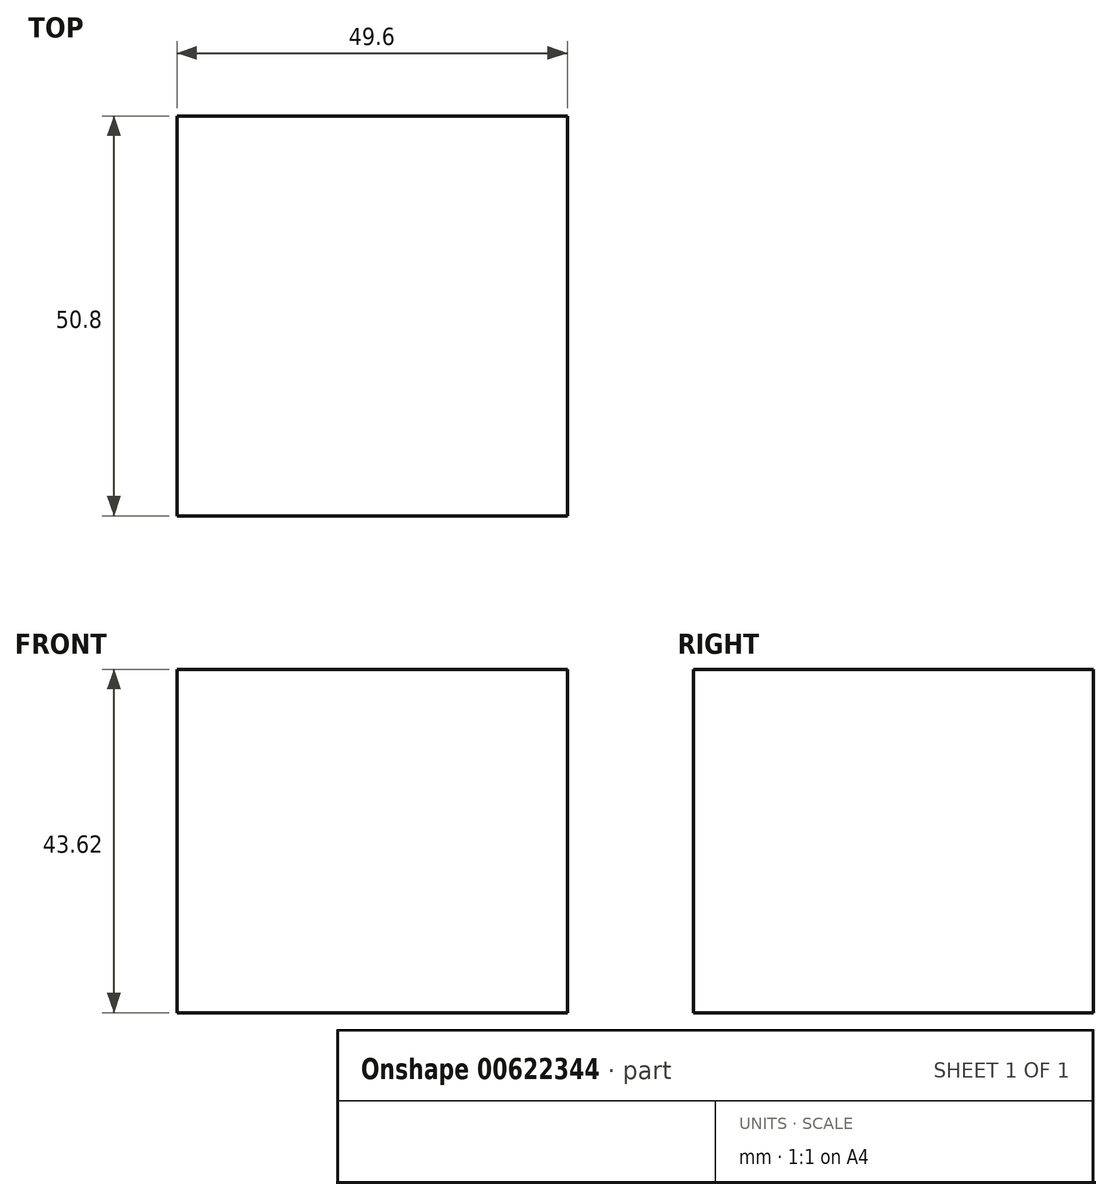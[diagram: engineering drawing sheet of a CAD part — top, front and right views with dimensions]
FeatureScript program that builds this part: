
annotation { "Feature Type Name" : "Feature", "Feature Type Description" : "" }
export const myFeature = defineFeature(function(context is Context, id is Id, definition is map)
    precondition{}
    {
        {
            var Q0;
            Q0=qCreatedBy(makeId("Front.planeOp"),FACE);
            var sketch = newSketch(context, id + "F0", { "sketchPlane" : qUnion([Q0])});
            skLineSegment(sketch, "E0.bottom", {"start": v(24.8, 21.81) * mm, "end": v(-24.8, 21.81) * mm});
            skLineSegment(sketch, "E0.top", {"start": v(24.8, -21.81) * mm, "end": v(-24.8, -21.81) * mm});
            skLineSegment(sketch, "E0.left", {"start": v(24.8, 21.81) * mm, "end": v(24.8, -21.81) * mm});
            skLineSegment(sketch, "E0.right", {"start": v(-24.8, 21.81) * mm, "end": v(-24.8, -21.81) * mm});
            skPoint(sketch, "E0.middle", {"position": v(0, 0) * mm});
            skSolve(sketch);
        }
        {
            var Q0;
            Q0=makeQuery(id+"F0.imprint","IMPRINT",FACE,{"disambiguationData":[TD([[makeQuery(id+"F0.imprint","IMPRINT",EDGE,{"derivedFrom":sQuery(id+"F0.wireOp",EDGE,"E0.bottom")}),1.0]])]});
            extrude(context, id + "F1", {"entities" : qUnion([Q0]), "endBound" : BoundingType.SYMMETRIC, "depth" : 50.8 * mm, "offsetDistance" : 25.4 * mm});
        }
    });
